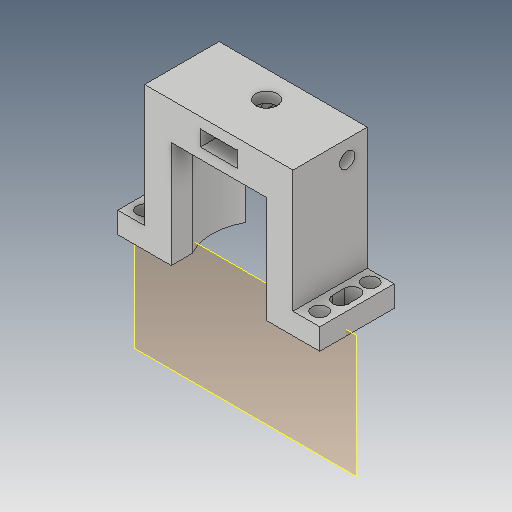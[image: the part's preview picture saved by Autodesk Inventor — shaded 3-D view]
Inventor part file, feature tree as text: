
AUTODESK INVENTOR PART (.ipt)
format: ipt  version: 2019.4 (Build 234330000, 330)  size: 225,792 bytes
history: native  units: mm
features: reference x6, extrude x4, sketch x4, other x3, plane x1, mirror x1, projected_geometry x1
ambient origin geometry x8: Origin, YZ Plane, XZ Plane, XY Plane, X Axis, Y Axis, Z Axis, Center Point
bodies: Solid1 (feature_tree)
feature tree (20):
  plane  "Work Plane1"
  extrude  "Extrusion1"  Depth=4.0mm
  extrude  "Extrusion2"  Depth=23.0mm
  extrude  "Extrusion3"  Depth=6.9mm
  extrude  "Extrusion4"  Depth=5.0mm TaperAngle=0.0deg
  mirror  "Mirror1"
  sketch  "Sketch1"  dims[d0=9.0mm d1=4.0mm]
  reference  "Reference1"
  sketch  "Sketch2"  dims[d2=5.0mm d3=23.0mm]
  reference  "Reference3"
  sketch  "Sketch3"  dims[d6=2.0mm d7=6.9mm]
  projected_geometry  "Projected Loop1"
  sketch  "Sketch4"  dims[d8=2.95mm d9=5.0mm d10=0.0mm d12=10.0mm d13=0.0mm d14=2.9mm d15=10.0mm d16=0.0mm d17=10.0mm d18=0.0mm d19=4.0mm d20=2.0mm d21=2.0mm d22=9.0mm d23=0.0mm]
  reference  "Reference6"
  reference  "Reference7"
  reference  "Reference8"
  reference  "Reference9"
  other  "Assembly_Opentrons_Autofocus_v2.iam"
  other  "01_Slide_camera_v1:1"
  other  "DIN 912 - replaced by DIN EN ISO 4762 M4 x 20:1"
